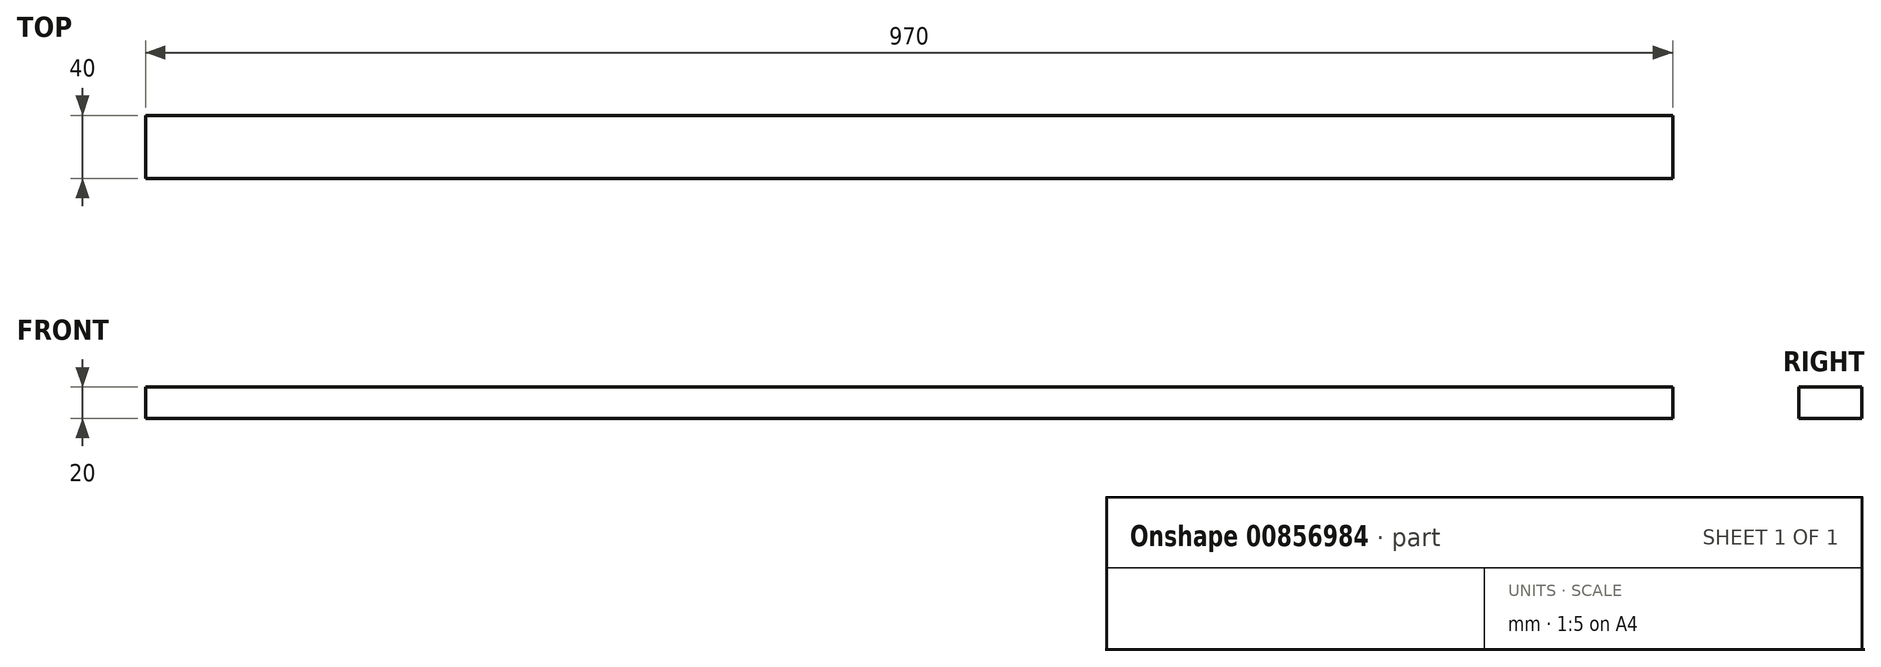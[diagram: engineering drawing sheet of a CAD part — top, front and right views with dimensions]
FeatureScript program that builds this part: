
annotation { "Feature Type Name" : "Feature", "Feature Type Description" : "" }
export const myFeature = defineFeature(function(context is Context, id is Id, definition is map)
    precondition{}
    {
        {
            var Q0;
            Q0=qCreatedBy(makeId("Right.planeOp"),FACE);
            var sketch = newSketch(context, id + "F0", { "sketchPlane" : qUnion([Q0])});
            skLineSegment(sketch, "E0.bottom", {"start": v(0, 0) * mm, "end": v(40, 0) * mm});
            skLineSegment(sketch, "E0.top", {"start": v(0, -20) * mm, "end": v(40, -20) * mm});
            skLineSegment(sketch, "E0.left", {"start": v(0, 0) * mm, "end": v(0, -20) * mm});
            skLineSegment(sketch, "E0.right", {"start": v(40, 0) * mm, "end": v(40, -20) * mm});
            skSolve(sketch);
        }
        {
            var Q0;
            Q0=makeQuery(id+"F0.imprint","IMPRINT",FACE,{"disambiguationData":[TD([[makeQuery(id+"F0.imprint","IMPRINT",EDGE,{"derivedFrom":sQuery(id+"F0.wireOp",EDGE,"E0.bottom")}),-1.0]])]});
            extrude(context, id + "F1", {"entities" : qUnion([Q0]), "depth" : 970 * mm, "offsetDistance" : 25 * mm});
        }
        {
            var Q0;
            Q0=makeQuery(id+"F1.opExtrude","SWEPT_FACE",FACE,{"disambiguationData":[OSD([sQuery(id+"F0.wireOp",EDGE,"E0.left")])]});
            var sketch = newSketch(context, id + "F2", { "sketchPlane" : qUnion([Q0])});
            skLineSegment(sketch, "E1", {"start": v(0, -10) * mm, "end": v(20, -10) * mm, "construction": true});
            skLineSegment(sketch, "E2", {"start": v(970, -10) * mm, "end": v(950, -10) * mm, "construction": true});
            skSolve(sketch);
        }
        {
            var Q0;
            Q0=makeQuery(id+"F1.opExtrude","SWEPT_FACE",FACE,{"disambiguationData":[OSD([sQuery(id+"F0.wireOp",EDGE,"E0.right")])]});
            var sketch = newSketch(context, id + "F3", { "sketchPlane" : qUnion([Q0])});
            skLineSegment(sketch, "E3", {"start": v(-970, -10) * mm, "end": v(-950, -10) * mm, "construction": true});
            skLineSegment(sketch, "E4", {"start": v(0, -10) * mm, "end": v(-20, -10) * mm, "construction": true});
            skSolve(sketch);
        }
    });
